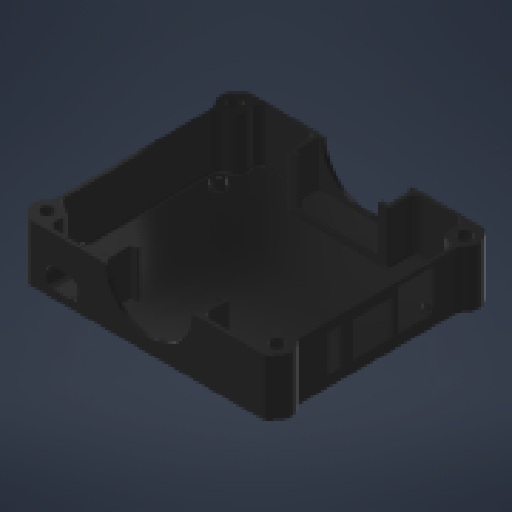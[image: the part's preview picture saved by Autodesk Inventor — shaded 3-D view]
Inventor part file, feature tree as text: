
AUTODESK INVENTOR PART (.ipt)
format: ipt  version: 2023 (Build 270158000, 158)  size: 844,800 bytes
history: native  units: in
note: dims shown in document units (in); Inventor stores cm internally (conversion verified against a paired STEP export)
features: reference x19, sketch x18, extrude x16, projected_geometry x5, other x4, plane x3, fillet x3, hole x2
ambient origin geometry x8: Origin, YZ Plane, XZ Plane, XY Plane, X Axis, Y Axis, Z Axis, Center Point
bodies: Solid1 (feature_tree)
feature tree (70):
  plane  "Work Plane1"
  extrude  "Extrusion1"  Depth=0.04in
  extrude  "Extrusion2"  Depth=0.5512in
  extrude  "Extrusion3"  Depth=0.065in
  extrude  "Extrusion4"  TaperAngle=0.0deg  [1 undecoded]
  extrude  "Extrusion5"  Depth=0.7874in TaperAngle=0.0deg
  extrude  "Extrusion6"  Depth=0.0787in TaperAngle=0.0deg
  sketch  "Sketch7"  dims[d16=0.1in d17=0.1181in d18=0.0in]
  plane  "Work Plane2"
  extrude  "Extrusion7"  Depth=0.1181in TaperAngle=0.0deg
  extrude  "Extrusion8"  Depth=0.1181in TaperAngle=0.0deg
  extrude  "Extrusion9"  Depth=0.1181in
  sketch  "Sketch10"  dims[d29=0.05in d30=0.15in]
  plane  "Work Plane3"
  extrude  "Extrusion10"  Depth=0.15in
  extrude  "Extrusion11"  Depth=1.7323in
  extrude  "Extrusion12"  Depth=0.4843in
  hole  "Hole1"  [1 undecoded]
  extrude  "Extrusion13"  Depth=0.1in
  fillet  "Fillet1"  Radius=0.063in
  extrude  "Extrusion14"  Depth=0.063in
  fillet  "Fillet2"  Radius=0.063in
  hole  "Hole2"  [1 undecoded]
  fillet  "Fillet3"  Radius=0.4724in
  extrude  "Extrusion15"  Depth=0.8661in
  extrude  "Extrusion16"  Depth=0.0312in
  sketch  "Sketch1"  dims[d0=0.04in d1=0.04in]
  reference  "Reference1"
  reference  "Reference2"
  sketch  "Sketch2"  dims[d2=0.5512in d3=0.5512in]
  projected_geometry  "Projected Loop1"
  sketch  "Sketch3"  dims[d5=0.065in d6=0.065in]
  sketch  "Sketch4"  dims[d7=0.065in d8=0.0in]
  reference  "Reference3"
  reference  "Reference4"
  reference  "Reference5"
  reference  "Reference6"
  sketch  "Sketch5"  dims[d9=0.065in d10=0.7874in d11=0.0in]
  reference  "Reference7"
  reference  "Reference8"
  reference  "Reference9"
  sketch  "Sketch6"  dims[d12=0.1969in d13=0.0in d14=0.0787in d15=0.0in]
  reference  "Reference10"
  reference  "Reference11"
  sketch  "Sketch8"  dims[d19=0.6378in d22=0.1181in d23=0.0in]
  projected_geometry  "Projected Loop2"
  sketch  "Sketch9"  dims[d25=0.1181in d26=0.0in d28=1.7853in]
  sketch  "Sketch11"  dims[d31=0.05in d32=1.7323in]
  sketch  "Sketch12"  dims[d33=0.8661in d34=0.4843in]
  sketch  "Sketch13"  dims[d35=1.0in d36=0.0in d45=1.0in d46=0.0in]
  sketch  "Sketch14"  dims[d47=0.1in d48=0.1in d49=0.063in]
  projected_geometry  "Projected Loop3"
  projected_geometry  "Projected Loop4"
  sketch  "Sketch15"  dims[d50=0.063in d51=0.063in d52=0.063in]
  sketch  "Sketch17"  dims[d53=1.4961in d54=1.0in d55=0.0in d56=0.4724in]
  sketch  "Sketch18"  dims[d57=1.7323in d58=0.8661in]
  projected_geometry  "Projected Loop5"
  sketch  "Sketch19"  dims[d59=1.0in d60=0.0in d62=0.063in d63=0.1in d64=0.063in d65=0.063in d66=0.063in d67=0.1in d68=1.0in d69=0.0in d70=1.4961in d71=1.0in d72=0.0in d73=0.0793in d74=0.197in d75=0.173in d76=0.079in d77=0.5635in d78=1.0in d79=0.8108in d80=0.0394in d81=0.625in d82=0.0in d83=0.125in d84=3.25in d85=4.0in d86=0.4724in d87=0.1969in d88=0.0in d89=0.125in d90=0.2283in d91=0.75in d92=0.3125in d93=0.164in d94=0.5635in d95=1.0in d96=0.8108in d97=0.0312in d98=1.0in d99=0.0in d100=0.3425in d101=0.2425in d102=0.1875in d103=1.0in d104=0.0in]
  reference  "Reference12"
  reference  "Reference13"
  reference  "Reference14"
  reference  "Reference15"
  reference  "Reference16"
  reference  "Reference17"
  reference  "Reference18"
  reference  "Reference19"
  other  "OrangePICover.iam"
  other  "OPi5_pcb_asm-0809:1"
  other  "orangepicover-001a:1"
  other  "Assembly10"
note: 3 required parameter values undecoded (feature->parameter linkage not recoverable at this tier; creation-order binding heuristic only, values carry confidence <= 0.55)
